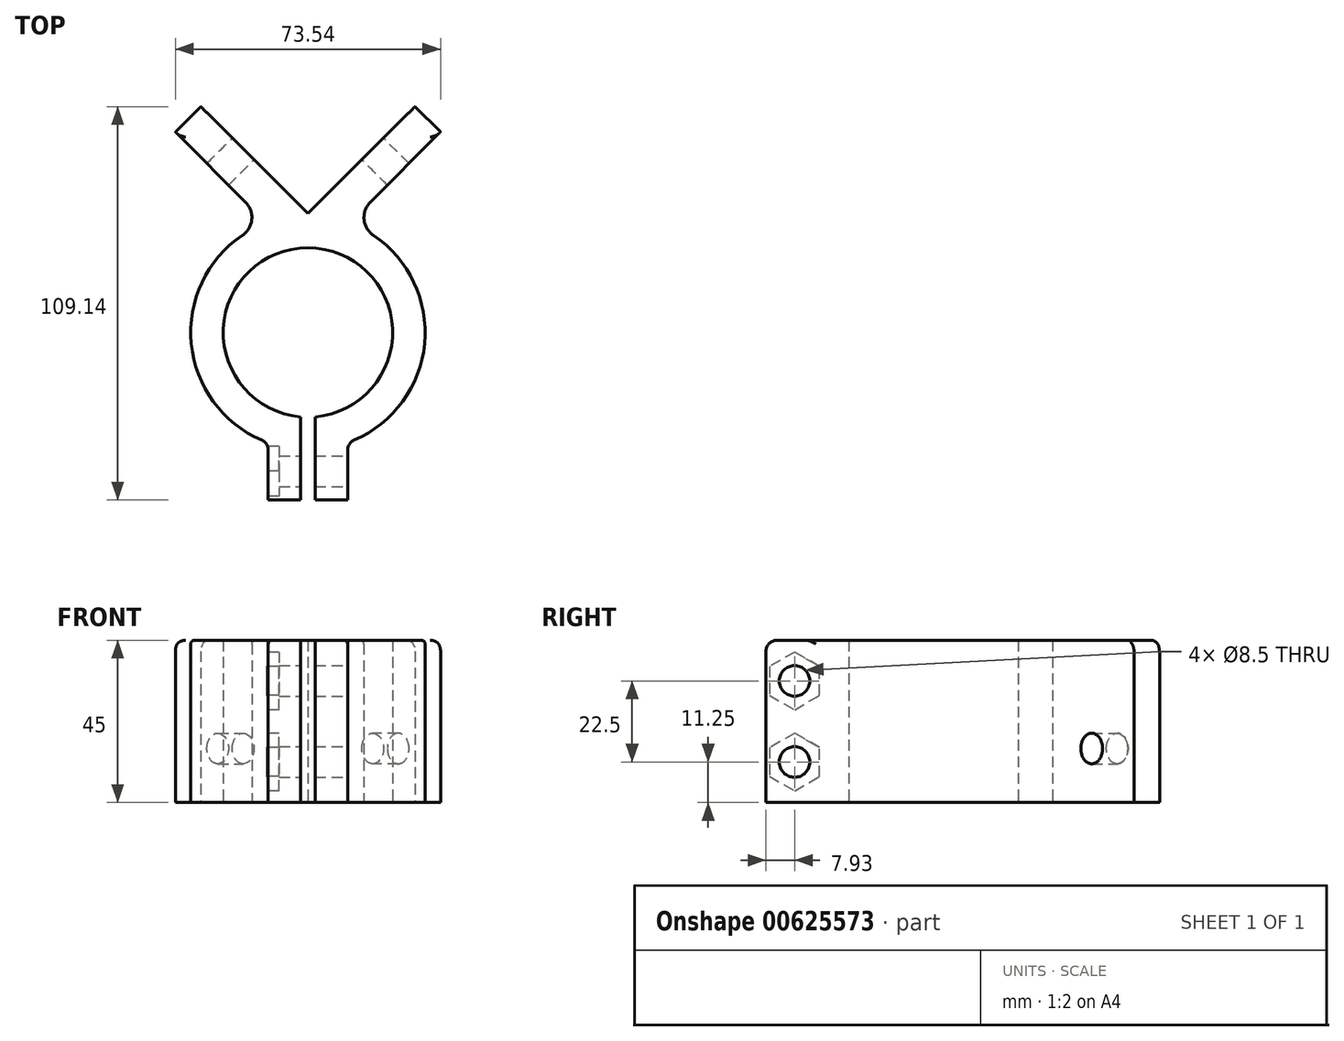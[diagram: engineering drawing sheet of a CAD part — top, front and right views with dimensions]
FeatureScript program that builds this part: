
annotation { "Feature Type Name" : "Feature", "Feature Type Description" : "" }
export const myFeature = defineFeature(function(context is Context, id is Id, definition is map)
    precondition{}
    {
        {
            var Q0;
            Q0=qCreatedBy(makeId("Top.planeOp"),FACE);
            var sketch = newSketch(context, id + "F0", { "sketchPlane" : qUnion([Q0])});
            skLineSegment(sketch, "E0", {"start": v(0, 0) * mm, "end": v(-29.7, 29.7) * mm});
            skLineSegment(sketch, "E1", {"start": v(0, 38.94) * mm, "end": v(0, 0) * mm, "construction": true});
            skLineSegment(sketch, "E2", {"start": v(-29.7, 29.7) * mm, "end": v(-36.77, 22.63) * mm});
            skLineSegment(sketch, "E3", {"start": v(-36.77, 22.63) * mm, "end": v(-11.53, -2.61) * mm});
            skLineSegment(sketch, "E4", {"start": v(0, 0) * mm, "end": v(0, -33) * mm, "construction": true});
            skArc(sketch, "E5", {"start": v(2, -56.41) * mm, "mid": v(0, -9.5) * mm, "end": v(-2, -56.41) * mm});
            skArc(sketch, "E6", {"start": v(2, -65.44) * mm, "mid": v(32.13, -37.87) * mm, "end": v(11.53, -2.61) * mm});
            skLineSegment(sketch, "E7", {"start": v(0, -33) * mm, "end": v(0, -65.5) * mm, "construction": true});
            skLineSegment(sketch, "E8", {"start": v(-2, -65.44) * mm, "end": v(-2, -79.44) * mm});
            skLineSegment(sketch, "E9", {"start": v(-2, -79.44) * mm, "end": v(-11, -79.44) * mm});
            skLineSegment(sketch, "E10", {"start": v(-11, -79.44) * mm, "end": v(-11, -63.58) * mm});
            skLineSegment(sketch, "E11.MirrorCS", {"start": v(2, -79.44) * mm, "end": v(11, -79.44) * mm});
            skLineSegment(sketch, "E12.MirrorCS", {"start": v(11, -79.44) * mm, "end": v(11, -63.58) * mm});
            skLineSegment(sketch, "E13.MirrorCS", {"start": v(2, -65.44) * mm, "end": v(2, -79.44) * mm});
            skLineSegment(sketch, "E14", {"start": v(-2, -65.44) * mm, "end": v(-2, -56.41) * mm});
            skLineSegment(sketch, "E15.MirrorCS", {"start": v(2, -65.44) * mm, "end": v(2, -56.41) * mm});
            skLineSegment(sketch, "E16.MirrorCS", {"start": v(29.7, 29.7) * mm, "end": v(36.77, 22.63) * mm});
            skLineSegment(sketch, "E17.MirrorCS", {"start": v(0, 0) * mm, "end": v(29.7, 29.7) * mm});
            skLineSegment(sketch, "E18.MirrorCS", {"start": v(36.77, 22.63) * mm, "end": v(11.53, -2.61) * mm});
            skPoint(sketch, "E19.orphan", {"position": v(0, -14.14) * mm});
            skArc(sketch, "E20.trimOffspring", {"start": v(-11.53, -2.61) * mm, "mid": v(-32.13, -37.87) * mm, "end": v(-2, -65.44) * mm});
            skLineSegment(sketch, "E21", {"start": v(-9, -54.7) * mm, "end": v(-5.5, -67.41) * mm});
            skLineSegment(sketch, "E22.MirrorCS", {"start": v(9, -54.7) * mm, "end": v(5.5, -67.41) * mm});
            skLineSegment(sketch, "E23", {"start": v(-5.5, -67.41) * mm, "end": v(5.5, -67.41) * mm});
            skSolve(sketch);
        }
        {
            var Q0;
            Q0=makeQuery(id+"F0.imprint","IMPRINT",FACE,{"disambiguationData":[TD([[makeQuery(id+"F0.imprint","IMPRINT",EDGE,{"derivedFrom":sQuery(id+"F0.wireOp",EDGE,"E0")}),1.0]])]});
            var Q1;
            {var subQ4=sQuery(id+"F0.wireOp",EDGE,"E9");Q1=makeQuery(id+"F0.imprint","IMPRINT",FACE,{"disambiguationData":[TD([[makeQuery(id+"F0.imprint","IMPRINT",EDGE,{"derivedFrom":subQ4}),-1.0]])]});}
            var Q2;
            {var subQ1=sQuery(id+"F0.wireOp",EDGE,"E11.MirrorCS");Q2=makeQuery(id+"F0.imprint","IMPRINT",FACE,{"disambiguationData":[TD([[makeQuery(id+"F0.imprint","IMPRINT",EDGE,{"derivedFrom":subQ1}),1.0]])]});}
            var Q3;
            {var subQ0=sQuery(id+"F0.wireOp",EDGE,"E14");Q3=makeQuery(id+"F0.imprint","IMPRINT",FACE,{"disambiguationData":[TD([[makeQuery(id+"F0.imprint","IMPRINT",EDGE,{"derivedFrom":subQ0}),1.0]])]});}
            var Q4;
            {var subQ0=sQuery(id+"F0.wireOp",EDGE,"E15.MirrorCS");Q4=makeQuery(id+"F0.imprint","IMPRINT",FACE,{"disambiguationData":[TD([[makeQuery(id+"F0.imprint","IMPRINT",EDGE,{"derivedFrom":subQ0}),-1.0]])]});}
            var Q5;
            {var subQ3=sQuery(id+"F0.wireOp",EDGE,"E23");var subQ5=sQuery(id+"F0.wireOp",EDGE,"E21");var subQ7=makeQuery(id+"F0.imprint","INTERSECT",VERTEX,{"derivedFrom":[subQ5,subQ3]});Q5=makeQuery(id+"F0.imprint","IMPRINT",FACE,{"disambiguationData":[TD([[makeQuery(id+"F0.imprint","IMPRINT",EDGE,{"disambiguationData":[TD([[subQ7,1.0]])],"derivedFrom":subQ5}),1.0]])]});}
            var Q6;
            {var subQ3=sQuery(id+"F0.wireOp",EDGE,"E22.MirrorCS");var subQ5=sQuery(id+"F0.wireOp",EDGE,"E23");var subQ6=makeQuery(id+"F0.imprint","INTERSECT",VERTEX,{"derivedFrom":[subQ3,subQ5]});Q6=makeQuery(id+"F0.imprint","IMPRINT",FACE,{"disambiguationData":[TD([[makeQuery(id+"F0.imprint","IMPRINT",EDGE,{"disambiguationData":[TD([[subQ6,1.0]])],"derivedFrom":subQ3}),-1.0]])]});}
            extrude(context, id + "F1", {"entities" : qUnion([Q0, Q1, Q2, Q3, Q4, Q5, Q6]), "depth" : 45 * mm, "offsetDistance" : 25 * mm});
        }
        {
            var Q0;
            Q0=makeQuery(id+"F1.opExtrude","SWEPT_FACE",FACE,{"disambiguationData":[OSD([sQuery(id+"F0.wireOp",EDGE,"E17.MirrorCS")])]});
            var sketch = newSketch(context, id + "F2", { "sketchPlane" : qUnion([Q0])});
            skLineSegment(sketch, "E24", {"start": v(0, 15) * mm, "end": v(-50.8, 15) * mm, "construction": true});
            skCircle(sketch, "E25", {"center": v(-25.4, 15) * mm, "radius": 4.25 * mm});
            skSolve(sketch);
        }
        {
            var Q0;
            Q0=qSketchRegion(id+"F2",true);
            extrude(context, id + "F3", {"entities" : qUnion([Q0]), "operationType" : NewBodyOperationType.REMOVE, "endBound" : BoundingType.UP_TO_NEXT, "oppositeDirection" : true, "depth" : 25 * mm, "offsetDistance" : 25 * mm});
        }
        {
            var Q0;
            Q0=makeQuery(id+"F1.opExtrude","SWEPT_FACE",FACE,{"disambiguationData":[OSD([sQuery(id+"F0.wireOp",EDGE,"E0")])]});
            var sketch = newSketch(context, id + "F4", { "sketchPlane" : qUnion([Q0])});
            skLineSegment(sketch, "E26", {"start": v(0, 15) * mm, "end": v(50.8, 15) * mm, "construction": true});
            skCircle(sketch, "E27", {"center": v(25.4, 15) * mm, "radius": 4.25 * mm});
            skSolve(sketch);
        }
        {
            var Q0;
            Q0=qSketchRegion(id+"F4",true);
            extrude(context, id + "F5", {"entities" : qUnion([Q0]), "operationType" : NewBodyOperationType.REMOVE, "endBound" : BoundingType.UP_TO_NEXT, "oppositeDirection" : true, "depth" : 25 * mm, "offsetDistance" : 25 * mm});
        }
        {
            var Q0;
            Q0=makeQuery(id+"F1.opExtrude","SWEPT_FACE",FACE,{"disambiguationData":[OSD([sQuery(id+"F0.wireOp",EDGE,"E12.MirrorCS")])]});
            var sketch = newSketch(context, id + "F6", { "sketchPlane" : qUnion([Q0])});
            skLineSegment(sketch, "E28", {"start": v(-71.51, 45) * mm, "end": v(-71.51, 0) * mm, "construction": true});
            skLineSegment(sketch, "E29", {"start": v(-79.44, 22.5) * mm, "end": v(-63.58, 22.5) * mm, "construction": true});
            skLineSegment(sketch, "E30", {"start": v(-79.44, 22.5) * mm, "end": v(-63.58, 45) * mm, "construction": true});
            skCircle(sketch, "E31", {"center": v(-71.51, 33.75) * mm, "radius": 4.25 * mm});
            skCircle(sketch, "E32.MirrorC", {"center": v(-71.51, 11.25) * mm, "radius": 4.25 * mm});
            skLineSegment(sketch, "E33.MirrorCS", {"start": v(-79.44, 22.5) * mm, "end": v(-63.58, 0) * mm, "construction": true});
            skSolve(sketch);
        }
        {
            var Q0;
            Q0=qSketchRegion(id+"F6",true);
            var Q1;
            Q1=makeQuery(id+"F1.opExtrude","SWEPT_FACE",FACE,{"disambiguationData":[OSD([sQuery(id+"F0.wireOp",EDGE,"E10")])]});
            extrude(context, id + "F7", {"entities" : qUnion([Q0]), "operationType" : NewBodyOperationType.REMOVE, "endBound" : BoundingType.UP_TO_SURFACE, "oppositeDirection" : true, "depth" : 25 * mm, "endBoundEntityFace" : qUnion([Q1]), "offsetDistance" : 25 * mm});
        }
        {
            var Q0;
            Q0=makeQuery(id+"F1.opExtrude","SWEPT_FACE",FACE,{"disambiguationData":[OSD([sQuery(id+"F0.wireOp",EDGE,"E10")])]});
            var sketch = newSketch(context, id + "F8", { "sketchPlane" : qUnion([Q0])});
            skCircle(sketch, "E34.cCircle", {"center": v(71.51, 33.75) * mm, "radius": 6.92 * mm, "construction": true});
            skLineSegment(sketch, "E34.0", {"start": v(71.51, 41.75) * mm, "end": v(78.44, 37.75) * mm});
            skLineSegment(sketch, "E34.1", {"start": v(78.44, 37.75) * mm, "end": v(78.44, 29.75) * mm});
            skLineSegment(sketch, "E34.2", {"start": v(78.44, 29.75) * mm, "end": v(71.51, 25.75) * mm});
            skLineSegment(sketch, "E34.3", {"start": v(71.51, 25.75) * mm, "end": v(64.59, 29.75) * mm});
            skLineSegment(sketch, "E34.4", {"start": v(64.59, 29.75) * mm, "end": v(64.59, 37.75) * mm});
            skLineSegment(sketch, "E34.5", {"start": v(64.59, 37.75) * mm, "end": v(71.51, 41.75) * mm});
            skPoint(sketch, "E34.0.midPoint", {"position": v(74.97, 39.75) * mm});
            skCircle(sketch, "E35.cCircle", {"center": v(71.51, 11.25) * mm, "radius": 6.92 * mm, "construction": true});
            skLineSegment(sketch, "E35.0", {"start": v(64.59, 15.25) * mm, "end": v(71.51, 19.25) * mm});
            skLineSegment(sketch, "E35.1", {"start": v(71.51, 19.25) * mm, "end": v(78.44, 15.25) * mm});
            skLineSegment(sketch, "E35.2", {"start": v(78.44, 15.25) * mm, "end": v(78.44, 7.25) * mm});
            skLineSegment(sketch, "E35.3", {"start": v(78.44, 7.25) * mm, "end": v(71.51, 3.25) * mm});
            skLineSegment(sketch, "E35.4", {"start": v(71.51, 3.25) * mm, "end": v(64.59, 7.25) * mm});
            skLineSegment(sketch, "E35.5", {"start": v(64.59, 7.25) * mm, "end": v(64.59, 15.25) * mm});
            skPoint(sketch, "E35.0.midPoint", {"position": v(68.05, 17.25) * mm});
            skSolve(sketch);
        }
        {
            var Q0;
            Q0=qSketchRegion(id+"F8",true);
            extrude(context, id + "F9", {"entities" : qUnion([Q0]), "operationType" : NewBodyOperationType.REMOVE, "oppositeDirection" : true, "depth" : 3 * mm, "offsetDistance" : 25 * mm});
        }
        {
            var Q0;
            Q0=makeQuery(id+"F1.opExtrude","SWEPT_EDGE",EDGE,{"disambiguationData":[OSD([sQuery(id+"F0.wireOp",EDGE,"E3"),sQuery(id+"F0.wireOp",EDGE,"E20.trimOffspring")])]});
            var Q1;
            Q1=makeQuery(id+"F1.opExtrude","SWEPT_EDGE",EDGE,{"disambiguationData":[OSD([sQuery(id+"F0.wireOp",EDGE,"E6"),sQuery(id+"F0.wireOp",EDGE,"E18.MirrorCS")])]});
            fillet(context, id + "F10", {"entities" : qUnion([Q0, Q1]), "radius" : 6 * mm, "tangentPropagation" : true, "allowEdgeOverflow" : false});
        }
        {
            var Q0;
            Q0=makeQuery(id+"F1.opExtrude","CAP_EDGE",EDGE,{"disambiguationData":[OSD([sQuery(id+"F0.wireOp",EDGE,"E9")])],"isStart":false});
            var Q1;
            Q1=makeQuery(id+"F1.opExtrude","CAP_EDGE",EDGE,{"disambiguationData":[OSD([sQuery(id+"F0.wireOp",EDGE,"E11.MirrorCS")])],"isStart":false});
            var Q2;
            Q2=makeQuery(id+"F1.opExtrude","CAP_EDGE",EDGE,{"disambiguationData":[OSD([sQuery(id+"F0.wireOp",EDGE,"E2")])],"isStart":false});
            var Q3;
            Q3=makeQuery(id+"F1.opExtrude","CAP_EDGE",EDGE,{"disambiguationData":[OSD([sQuery(id+"F0.wireOp",EDGE,"E16.MirrorCS")])],"isStart":false});
            var Q4;
            Q4=makeQuery(id+"F1.opExtrude","SWEPT_EDGE",EDGE,{"disambiguationData":[OSD([sQuery(id+"F0.wireOp",EDGE,"E10"),sQuery(id+"F0.wireOp",EDGE,"E20.trimOffspring")])]});
            var Q5;
            Q5=makeQuery(id+"F1.opExtrude","SWEPT_EDGE",EDGE,{"disambiguationData":[OSD([sQuery(id+"F0.wireOp",EDGE,"E6"),sQuery(id+"F0.wireOp",EDGE,"E12.MirrorCS")])]});
            fillet(context, id + "F11", {"entities" : qUnion([Q0, Q1, Q2, Q3, Q4, Q5]), "radius" : 3 * mm, "tangentPropagation" : true, "allowEdgeOverflow" : false});
        }
        {
            var Q0;
            Q0=makeQuery(id+"F1.opExtrude","CAP_EDGE",EDGE,{"disambiguationData":[OSD([sQuery(id+"F0.wireOp",EDGE,"E6")])],"isStart":false});
            var Q1;
            {var subQ0=sQuery(id+"F0.wireOp",EDGE,"E12.MirrorCS");var subQ1=sQuery(id+"F0.wireOp",EDGE,"E6");Q1=makeQuery(id+"F11.opFillet","BLEND_EDGE",EDGE,{"blendedFrom":[makeQuery(id+"F1.opExtrude","SWEPT_EDGE",EDGE,{"disambiguationData":[OSD([subQ1,subQ0])]}),makeQuery(id+"F1.opExtrude","CAP_FACE",FACE,{"disambiguationData":[OSD([sQuery(id+"F0.wireOp",EDGE,"E0"),sQuery(id+"F0.wireOp",EDGE,"E2"),sQuery(id+"F0.wireOp",EDGE,"E3"),sQuery(id+"F0.wireOp",EDGE,"E5"),subQ1,sQuery(id+"F0.wireOp",EDGE,"E8"),sQuery(id+"F0.wireOp",EDGE,"E9"),sQuery(id+"F0.wireOp",EDGE,"E10"),sQuery(id+"F0.wireOp",EDGE,"E11.MirrorCS"),subQ0,sQuery(id+"F0.wireOp",EDGE,"E13.MirrorCS"),sQuery(id+"F0.wireOp",EDGE,"E16.MirrorCS"),sQuery(id+"F0.wireOp",EDGE,"E17.MirrorCS"),sQuery(id+"F0.wireOp",EDGE,"E18.MirrorCS"),sQuery(id+"F0.wireOp",EDGE,"E20.trimOffspring"),sQuery(id+"F0.wireOp",EDGE,"E21"),sQuery(id+"F0.wireOp",EDGE,"E22.MirrorCS"),sQuery(id+"F0.wireOp",EDGE,"E23")])],"isStart":false})],"blendedInto":[makeQuery(id+"F1.opExtrude","CAP_FACE",FACE,{"disambiguationData":[OSD([sQuery(id+"F0.wireOp",EDGE,"E0"),sQuery(id+"F0.wireOp",EDGE,"E2"),sQuery(id+"F0.wireOp",EDGE,"E3"),sQuery(id+"F0.wireOp",EDGE,"E5"),subQ1,sQuery(id+"F0.wireOp",EDGE,"E8"),sQuery(id+"F0.wireOp",EDGE,"E9"),sQuery(id+"F0.wireOp",EDGE,"E10"),sQuery(id+"F0.wireOp",EDGE,"E11.MirrorCS"),subQ0,sQuery(id+"F0.wireOp",EDGE,"E13.MirrorCS"),sQuery(id+"F0.wireOp",EDGE,"E16.MirrorCS"),sQuery(id+"F0.wireOp",EDGE,"E17.MirrorCS"),sQuery(id+"F0.wireOp",EDGE,"E18.MirrorCS"),sQuery(id+"F0.wireOp",EDGE,"E20.trimOffspring"),sQuery(id+"F0.wireOp",EDGE,"E21"),sQuery(id+"F0.wireOp",EDGE,"E22.MirrorCS"),sQuery(id+"F0.wireOp",EDGE,"E23")])],"isStart":false})]});}
            var Q2;
            {var subQ0=sQuery(id+"F0.wireOp",EDGE,"E20.trimOffspring");var subQ1=sQuery(id+"F0.wireOp",EDGE,"E3");Q2=makeQuery(id+"F10.opFillet","BLEND_EDGE",EDGE,{"blendedFrom":[makeQuery(id+"F1.opExtrude","SWEPT_EDGE",EDGE,{"disambiguationData":[OSD([subQ1,subQ0])]}),makeQuery(id+"F1.opExtrude","CAP_FACE",FACE,{"disambiguationData":[OSD([sQuery(id+"F0.wireOp",EDGE,"E0"),sQuery(id+"F0.wireOp",EDGE,"E2"),subQ1,sQuery(id+"F0.wireOp",EDGE,"E5"),sQuery(id+"F0.wireOp",EDGE,"E6"),sQuery(id+"F0.wireOp",EDGE,"E8"),sQuery(id+"F0.wireOp",EDGE,"E9"),sQuery(id+"F0.wireOp",EDGE,"E10"),sQuery(id+"F0.wireOp",EDGE,"E11.MirrorCS"),sQuery(id+"F0.wireOp",EDGE,"E12.MirrorCS"),sQuery(id+"F0.wireOp",EDGE,"E13.MirrorCS"),sQuery(id+"F0.wireOp",EDGE,"E16.MirrorCS"),sQuery(id+"F0.wireOp",EDGE,"E17.MirrorCS"),sQuery(id+"F0.wireOp",EDGE,"E18.MirrorCS"),subQ0,sQuery(id+"F0.wireOp",EDGE,"E21"),sQuery(id+"F0.wireOp",EDGE,"E22.MirrorCS"),sQuery(id+"F0.wireOp",EDGE,"E23")])],"isStart":false})],"blendedInto":[makeQuery(id+"F1.opExtrude","CAP_FACE",FACE,{"disambiguationData":[OSD([sQuery(id+"F0.wireOp",EDGE,"E0"),sQuery(id+"F0.wireOp",EDGE,"E2"),subQ1,sQuery(id+"F0.wireOp",EDGE,"E5"),sQuery(id+"F0.wireOp",EDGE,"E6"),sQuery(id+"F0.wireOp",EDGE,"E8"),sQuery(id+"F0.wireOp",EDGE,"E9"),sQuery(id+"F0.wireOp",EDGE,"E10"),sQuery(id+"F0.wireOp",EDGE,"E11.MirrorCS"),sQuery(id+"F0.wireOp",EDGE,"E12.MirrorCS"),sQuery(id+"F0.wireOp",EDGE,"E13.MirrorCS"),sQuery(id+"F0.wireOp",EDGE,"E16.MirrorCS"),sQuery(id+"F0.wireOp",EDGE,"E17.MirrorCS"),sQuery(id+"F0.wireOp",EDGE,"E18.MirrorCS"),subQ0,sQuery(id+"F0.wireOp",EDGE,"E21"),sQuery(id+"F0.wireOp",EDGE,"E22.MirrorCS"),sQuery(id+"F0.wireOp",EDGE,"E23")])],"isStart":false})]});}
            var Q3;
            Q3=makeQuery(id+"F1.opExtrude","CAP_EDGE",EDGE,{"disambiguationData":[OSD([sQuery(id+"F0.wireOp",EDGE,"E3")])],"isStart":false});
            var Q4;
            Q4=makeQuery(id+"F1.opExtrude","CAP_EDGE",EDGE,{"disambiguationData":[OSD([sQuery(id+"F0.wireOp",EDGE,"E18.MirrorCS")])],"isStart":false});
            var Q5;
            {var subQ0=sQuery(id+"F0.wireOp",EDGE,"E18.MirrorCS");var subQ1=sQuery(id+"F0.wireOp",EDGE,"E6");Q5=makeQuery(id+"F10.opFillet","BLEND_EDGE",EDGE,{"blendedFrom":[makeQuery(id+"F1.opExtrude","SWEPT_EDGE",EDGE,{"disambiguationData":[OSD([subQ1,subQ0])]}),makeQuery(id+"F1.opExtrude","CAP_FACE",FACE,{"disambiguationData":[OSD([sQuery(id+"F0.wireOp",EDGE,"E0"),sQuery(id+"F0.wireOp",EDGE,"E2"),sQuery(id+"F0.wireOp",EDGE,"E3"),sQuery(id+"F0.wireOp",EDGE,"E5"),subQ1,sQuery(id+"F0.wireOp",EDGE,"E8"),sQuery(id+"F0.wireOp",EDGE,"E9"),sQuery(id+"F0.wireOp",EDGE,"E10"),sQuery(id+"F0.wireOp",EDGE,"E11.MirrorCS"),sQuery(id+"F0.wireOp",EDGE,"E12.MirrorCS"),sQuery(id+"F0.wireOp",EDGE,"E13.MirrorCS"),sQuery(id+"F0.wireOp",EDGE,"E16.MirrorCS"),sQuery(id+"F0.wireOp",EDGE,"E17.MirrorCS"),subQ0,sQuery(id+"F0.wireOp",EDGE,"E20.trimOffspring"),sQuery(id+"F0.wireOp",EDGE,"E21"),sQuery(id+"F0.wireOp",EDGE,"E22.MirrorCS"),sQuery(id+"F0.wireOp",EDGE,"E23")])],"isStart":false})],"blendedInto":[makeQuery(id+"F1.opExtrude","CAP_FACE",FACE,{"disambiguationData":[OSD([sQuery(id+"F0.wireOp",EDGE,"E0"),sQuery(id+"F0.wireOp",EDGE,"E2"),sQuery(id+"F0.wireOp",EDGE,"E3"),sQuery(id+"F0.wireOp",EDGE,"E5"),subQ1,sQuery(id+"F0.wireOp",EDGE,"E8"),sQuery(id+"F0.wireOp",EDGE,"E9"),sQuery(id+"F0.wireOp",EDGE,"E10"),sQuery(id+"F0.wireOp",EDGE,"E11.MirrorCS"),sQuery(id+"F0.wireOp",EDGE,"E12.MirrorCS"),sQuery(id+"F0.wireOp",EDGE,"E13.MirrorCS"),sQuery(id+"F0.wireOp",EDGE,"E16.MirrorCS"),sQuery(id+"F0.wireOp",EDGE,"E17.MirrorCS"),subQ0,sQuery(id+"F0.wireOp",EDGE,"E20.trimOffspring"),sQuery(id+"F0.wireOp",EDGE,"E21"),sQuery(id+"F0.wireOp",EDGE,"E22.MirrorCS"),sQuery(id+"F0.wireOp",EDGE,"E23")])],"isStart":false})]});}
            var Q6;
            {var subQ0=sQuery(id+"F0.wireOp",EDGE,"E20.trimOffspring");var subQ1=sQuery(id+"F0.wireOp",EDGE,"E10");Q6=makeQuery(id+"F11.opFillet","BLEND_EDGE",EDGE,{"blendedFrom":[makeQuery(id+"F1.opExtrude","SWEPT_EDGE",EDGE,{"disambiguationData":[OSD([subQ1,subQ0])]}),makeQuery(id+"F1.opExtrude","CAP_FACE",FACE,{"disambiguationData":[OSD([sQuery(id+"F0.wireOp",EDGE,"E0"),sQuery(id+"F0.wireOp",EDGE,"E2"),sQuery(id+"F0.wireOp",EDGE,"E3"),sQuery(id+"F0.wireOp",EDGE,"E5"),sQuery(id+"F0.wireOp",EDGE,"E6"),sQuery(id+"F0.wireOp",EDGE,"E8"),sQuery(id+"F0.wireOp",EDGE,"E9"),subQ1,sQuery(id+"F0.wireOp",EDGE,"E11.MirrorCS"),sQuery(id+"F0.wireOp",EDGE,"E12.MirrorCS"),sQuery(id+"F0.wireOp",EDGE,"E13.MirrorCS"),sQuery(id+"F0.wireOp",EDGE,"E16.MirrorCS"),sQuery(id+"F0.wireOp",EDGE,"E17.MirrorCS"),sQuery(id+"F0.wireOp",EDGE,"E18.MirrorCS"),subQ0,sQuery(id+"F0.wireOp",EDGE,"E21"),sQuery(id+"F0.wireOp",EDGE,"E22.MirrorCS"),sQuery(id+"F0.wireOp",EDGE,"E23")])],"isStart":false})],"blendedInto":[makeQuery(id+"F1.opExtrude","CAP_FACE",FACE,{"disambiguationData":[OSD([sQuery(id+"F0.wireOp",EDGE,"E0"),sQuery(id+"F0.wireOp",EDGE,"E2"),sQuery(id+"F0.wireOp",EDGE,"E3"),sQuery(id+"F0.wireOp",EDGE,"E5"),sQuery(id+"F0.wireOp",EDGE,"E6"),sQuery(id+"F0.wireOp",EDGE,"E8"),sQuery(id+"F0.wireOp",EDGE,"E9"),subQ1,sQuery(id+"F0.wireOp",EDGE,"E11.MirrorCS"),sQuery(id+"F0.wireOp",EDGE,"E12.MirrorCS"),sQuery(id+"F0.wireOp",EDGE,"E13.MirrorCS"),sQuery(id+"F0.wireOp",EDGE,"E16.MirrorCS"),sQuery(id+"F0.wireOp",EDGE,"E17.MirrorCS"),sQuery(id+"F0.wireOp",EDGE,"E18.MirrorCS"),subQ0,sQuery(id+"F0.wireOp",EDGE,"E21"),sQuery(id+"F0.wireOp",EDGE,"E22.MirrorCS"),sQuery(id+"F0.wireOp",EDGE,"E23")])],"isStart":false})]});}
            var Q7;
            Q7=makeQuery(id+"F1.opExtrude","CAP_EDGE",EDGE,{"disambiguationData":[OSD([sQuery(id+"F0.wireOp",EDGE,"E20.trimOffspring")])],"isStart":false});
            fillet(context, id + "F12", {"entities" : qUnion([Q0, Q1, Q2, Q3, Q4, Q5, Q6, Q7]), "radius" : 1 * mm, "allowEdgeOverflow" : false});
        }
    });
